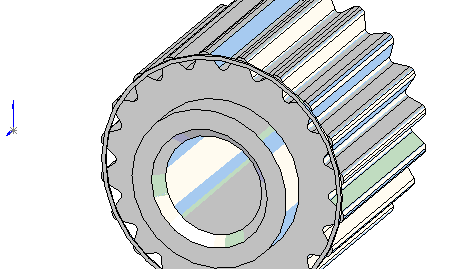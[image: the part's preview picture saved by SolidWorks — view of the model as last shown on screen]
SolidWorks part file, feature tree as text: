
SOLIDWORKS PART (.sldprt)
format: sldprt  version: not decoded by parser v0  size: 462,848 bytes
history: native  units: mm
features: plane x2, sketch x1, revolve x1, cut_extrude x1, fillet x1, pattern_circular x1, chamfer x1, extrude x1 + 7 further entries (+7 scaffold rows collapsed)
feature tree (23):
  scaffold x7  (default folders/planes/origin — collapsed)
  "Corps de surface"
  plane  "Face"
  "Dessus"
  "Droite"
  sketch  "Esquisse1"
  "param"
  plane  "gss_2demu_pline1"
  "param"
  revolve  "Révolution1"  Angle=360deg
  "Esquisse2"
  cut_extrude  "Enlèv. mat.-Extru.1"  [1 undecoded]
  fillet  "Congé1"  Radius=0.25mm
  pattern_circular  "Répétition circulaire1"  Count=20 Angle=360deg
  chamfer  "Chanfrein1"  Distance=0.5mm Angle=45deg
  "Esquisse3"
  extrude  "Extrusion1"  Depth=0.1mm
decode coverage: 5 of 7 modeling features carry decoded parameters; 7 rows unclassified (native names shown)
note: 1 parameter value undecoded
note: suppression state not decoded; provenance and decode notes live in map.json
